# Revit family: Thorn AXYL ECHO CEILING
name_source: partatom
category: Lighting Fixtures
units: mm (PartAtom-declared; Revit-internal decimal feet)

## family parameters
Cut with Voids When Loaded = Yes
Host = Face
Light Source = Yes
Maintain Annotation Orientation = No
Part Type = Normal
Room Calculation Point = Yes
Round Connector Dimension = Use Diameter
Shared = No

## types (1)
- Thorn AXYL ECHO CEILING
    Apparent Load = 22 VA
    Assembly Code = PR_70_70_49_02
    Color Filter = 16777215
    Default Elevation = 0 mm  [stored 0 ft]
    Description = LED Luminaire for decorative facade lighting
    Dimming Lamp Color Temperature Shift = <None>
    Emit Shape Visible in Rendering = No
    Emit from Rectangle Length = 123 mm
    Emit from Rectangle Width = 123 mm
    Export Type to IFC As = IfcLightFixtureType
    Housing Medium = Yes
    Housing Small = No
    Lamp = LED
    Light Source Edge Offset = 16 mm  [stored 0.0524934 ft]
    Luminaire Height = 155 mm  [stored 0.50853 ft]
    Luminaire Length = 155 mm  [stored 0.50853 ft]
    Luminaire Size = Thorn-Parts-Axyl-Echo-Body : Medium Size Ceiling
    Luminaire Width = 155 mm  [stored 0.50853 ft]
    Manufacturer = Thorn Lighting
    Material Housing = Thorn-Aluminium-RAL 7016-Anthracite Grey
    Medium Size = Thorn-Parts-Axyl-Echo-Body : Medium Size Ceiling
    Model = 96801400
    Photometric Web File = 96801400_(STD).IES
    Power Factor = 0.95
    Small Size = Thorn-Parts-Axyl-Echo-Body : Small Size Ceiling
    Tilt Angle = -90.00°
    Type IFC Predefined Type = DIRECTIONSOURCE
    Type Image = TLG_AXYL_F_ECHO_M_CEI_9L_HFX_ANT.jpg
    URL = https://www.thornlighting.com
    Wattage = 21 W

note: [stored X ft] marks values corroborated as IEEE doubles in the binary element streams (Revit-internal decimal feet)

## geometry (parser evidence)
native form markers: Sweep x5
no freeform markers — native parametric forms only
